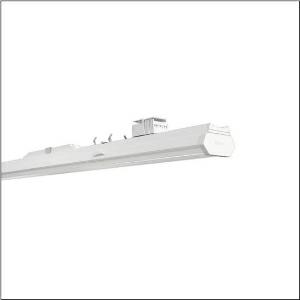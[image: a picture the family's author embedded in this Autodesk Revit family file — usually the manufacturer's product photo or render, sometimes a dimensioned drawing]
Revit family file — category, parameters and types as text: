
# Revit family: licross_21_protected_ho_52tp12dn4dxm
name_source: partatom
category: Lighting Fixtures
units: mm (PartAtom-declared; Revit-internal decimal feet)

## family parameters
Cut with Voids When Loaded = No
Host = Face
Light Source = No
Part Type = Normal
Room Calculation Point = No
Round Connector Dimension = Use Diameter
Shared = No

## types (1)
- --- (1 x LED, 13000 lm, 74.3 W, 4000K)
    Apparent Load = 74 VA
    CIE Flux Codes = 70 91 97 98 100
    Color Rendering = 80
    Color Temperature = 4000K
    Default Elevation = 1800 mm
    Description = Licross 21 Protected HO, luminaire insert, of sheet steel, galvanised, coil coated, white, length: 1.500mm, width: 90mm, height: 103mm, LED rated luminous flux: 13.000lm, light colour: 840, SDCM (Standard Deviation of Colour Matching)MacAdam ≤ 3 SDCM (initial), control gear: DALI 2, with plug, 5-pole, with phase selection, mains connection: 220..240V, AC, 50/60Hz, rated input power: 74W, internal wiring halogen-free, primary light control with lens, of plastic, primary optical cover: cover, of PMMA, light emission: direct distribution, primary light characteristic: symmetric, protection rating (complete): IP64, insulation class (complete): insulation class I (protective earthing), certification: CE, ENEC, VDE, UKCA, protection symbol: D if used in an environment with conductive dust loads with corresponding accessories, impact resistance: IK06, permissible ambient temperature for indoor applications: -25..+40°C, corresponds to IFS (International Featured Standards) requirements for safety and quality in the food industry, reducing of maximum allowable ambient temperature of 5°C with ceiling mounting, LABS conformity tested according to VDMA 24364:2018-05, The light source and the operating device comply with the requirements of the Ecodesign Regulation (EU) 2019/2020 and are replaceable in accordance with this regulation, packaging unit: 1 piece
    Height = 92 mm
    Lamp = 1 x LED
    Lamp Light Flux = 13000 lm
    Lamp Power = 74.3 W
    Lamp count = 1
    Length = 1500 mm
    Luminous efficacy = 175 lm/W
    Manufacturer = Siteco
    ModVariant = No
    Model = 52TP12DN4DXM
    Mounting Place = Ceiling
    Mounting Type = Pendant
    Number of Poles = 1
    OnlyDefault = Yes
    Power Factor = 1
    Product Name = Licross 21 Protected HO
    Product group = luminaire insert | ceiling pendant
    ProductGroupID = 901
    Protection Class = Protection class I
    Protection Degree = IP 64
    RLX_Detail_Level = 1
    RLX_Emergency_Light_Flux = 0 lm
    RLX_Emergency_Type = 0
    RLX_Emergency_Type_DB = No
    RlxData = <blob elided: 24765 chars, md5=36fc3850>
    Socket = socket
    Standby Power = 0 W
    System Light Flux = 13000 lm
    System Power = 74 W
    Type Comments = factory setting: luminous flux: 100 % | dim-lin: 254 | 424 mA
    Type Image = l_1256148.jpg
    URL = http://relux.com
    VarID = @adj_128971
    Voltage = 0 V
    Weight = 0.00 kg
    Width = 88 mm

## geometry (parser evidence)
native form markers: Blend x4, Sweep x10
no freeform markers — native parametric forms only
